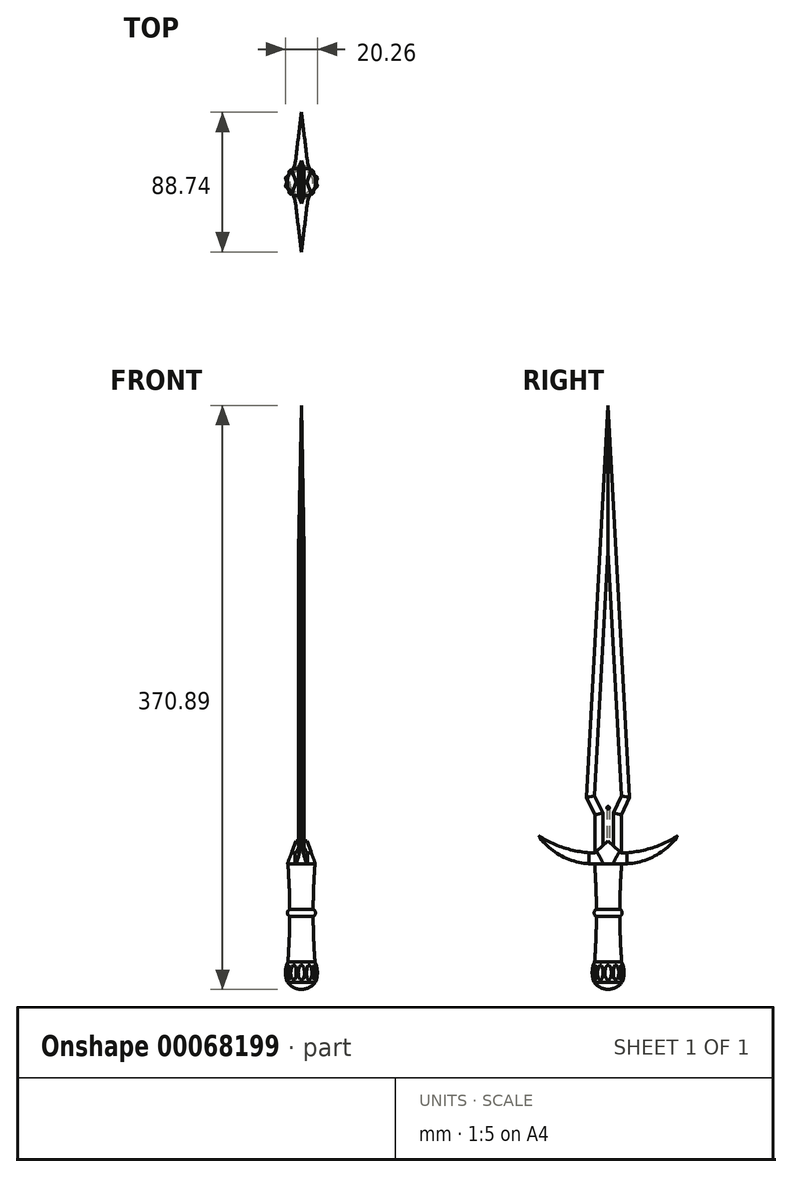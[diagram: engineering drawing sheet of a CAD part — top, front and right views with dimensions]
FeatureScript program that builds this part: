
annotation { "Feature Type Name" : "Feature", "Feature Type Description" : "" }
export const myFeature = defineFeature(function(context is Context, id is Id, definition is map)
    precondition{}
    {
        {
            var Q0;
            Q0=qCreatedBy(makeId("Right.planeOp"),FACE);
            var sketch = newSketch(context, id + "F0", { "sketchPlane" : qUnion([Q0])});
            skLineSegment(sketch, "E0", {"start": v(0, 0) * mm, "end": v(0, -62.4) * mm});
            skLineSegment(sketch, "E1", {"start": v(0, -62.4) * mm, "end": v(-8.58, -62.4) * mm});
            skLineSegment(sketch, "E2", {"start": v(0, 0) * mm, "end": v(-8.58, 0) * mm});
            skLineSegment(sketch, "E3.MirrorCS", {"start": v(0, 0) * mm, "end": v(8.58, 0) * mm});
            skLineSegment(sketch, "E4.MirrorCS", {"start": v(0, -62.4) * mm, "end": v(8.58, -62.4) * mm});
            skPoint(sketch, "E5.MirrorCS.end.orphan", {"position": v(8.58, 0) * mm});
            skPoint(sketch, "E5.MirrorCS.start.orphan", {"position": v(8.58, -62.4) * mm});
            skArc(sketch, "E6", {"start": v(8.58, 0) * mm, "mid": v(7.46, -31.2) * mm, "end": v(8.58, -62.4) * mm});
            skArc(sketch, "E7.MirrorCS", {"start": v(-8.58, 0) * mm, "mid": v(-7.46, -31.2) * mm, "end": v(-8.58, -62.4) * mm});
            skSolve(sketch);
        }
        {
            var Q0;
            Q0=makeQuery(id+"F0.imprint","IMPRINT",FACE,{"disambiguationData":[TD([[makeQuery(id+"F0.imprint","IMPRINT",EDGE,{"derivedFrom":sQuery(id+"F0.wireOp",EDGE,"E0")}),-1.0]])]});
            var Q1;
            Q1=sQuery(id+"F0.wireOp",EDGE,"E0");
            revolve(context, id + "F1", {"entities" : qUnion([Q0]), "axis" : qUnion([Q1]), "revolveType" : RevolveType.FULL});
        }
        {
            var Q0;
            Q0=qCreatedBy(makeId("Front.planeOp"),FACE);
            var sketch = newSketch(context, id + "F2", { "sketchPlane" : qUnion([Q0])});
            skArc(sketch, "E8", {"start": v(-8.58, -62.4) * mm, "mid": v(-6.45, -31.2) * mm, "end": v(-8.58, 0) * mm});
            skCircle(sketch, "E9", {"center": v(-6.45, -31.2) * mm, "radius": 2.43 * mm});
            skLineSegment(sketch, "E10", {"start": v(0, 0) * mm, "end": v(0, -35.93) * mm});
            skSolve(sketch);
        }
        {
            var Q0;
            {var subQ0=sQuery(id+"F2.wireOp",EDGE,"E9");var subQ1=sQuery(id+"F2.wireOp",EDGE,"E8");var subQ2=makeQuery(id+"F2.imprint","INTERSECT",VERTEX,{"disambiguationData":[OD(0.0)],"derivedFrom":[subQ1,subQ0]});Q0=makeQuery(id+"F2.imprint","IMPRINT",FACE,{"disambiguationData":[TD([[makeQuery(id+"F2.imprint","IMPRINT",EDGE,{"disambiguationData":[TD([[subQ2,-1.0]])],"derivedFrom":subQ1}),1.0]])]});}
            var Q1;
            Q1=sQuery(id+"F2.wireOp",EDGE,"E10");
            revolve(context, id + "F3", {"operationType" : NewBodyOperationType.ADD, "entities" : qUnion([Q0]), "axis" : qUnion([Q1]), "revolveType" : RevolveType.FULL});
        }
        {
            var Q0;
            Q0=qCreatedBy(makeId("Front.planeOp"),FACE);
            var sketch = newSketch(context, id + "F4", { "sketchPlane" : qUnion([Q0])});
            skLineSegment(sketch, "E11.0", {"start": v(-8.58, -62.4) * mm, "end": v(8.58, -62.4) * mm});
            skArc(sketch, "E12", {"start": v(-8.58, -62.4) * mm, "mid": v(-10.33, -68.79) * mm, "end": v(-8.87, -75.25) * mm});
            skLineSegment(sketch, "E13", {"start": v(0, -62.4) * mm, "end": v(0, -66.92) * mm});
            skArc(sketch, "E14.MirrorCS", {"start": v(8.58, -62.4) * mm, "mid": v(10.33, -68.79) * mm, "end": v(8.87, -75.25) * mm});
            skArc(sketch, "E15", {"start": v(-8.87, -75.25) * mm, "mid": v(0, -79.74) * mm, "end": v(8.87, -75.25) * mm});
            skLineSegment(sketch, "E16", {"start": v(0, -66.92) * mm, "end": v(0, -79.74) * mm});
            skSolve(sketch);
        }
        {
            var Q0;
            {var subQ1=sQuery(id+"F4.wireOp",EDGE,"E12");Q0=makeQuery(id+"F4.imprint","IMPRINT",FACE,{"disambiguationData":[TD([[makeQuery(id+"F4.imprint","IMPRINT",EDGE,{"derivedFrom":subQ1}),1.0]])]});}
            var Q1;
            Q1=sQuery(id+"F4.wireOp",EDGE,"E16");
            revolve(context, id + "F5", {"entities" : qUnion([Q0]), "axis" : qUnion([Q1]), "revolveType" : RevolveType.FULL});
        }
        {
            var Q0;
            Q0=makeQuery(id+"F5.opRevolve","SWEPT_FACE",FACE,{"disambiguationData":[OSD([sQuery(id+"F4.wireOp",EDGE,"E11.0")])]});
            var sketch = newSketch(context, id + "F6", { "sketchPlane" : qUnion([Q0])});
            skCircle(sketch, "E17.0.0", {"center": v(0, 0) * mm, "radius": 8.58 * mm});
            skCircle(sketch, "E18", {"center": v(0, 0) * mm, "radius": 10.33 * mm});
            skArc(sketch, "E19", {"start": v(-2.02, 10.13) * mm, "mid": v(0, 9.5) * mm, "end": v(2.02, 10.13) * mm});
            skArc(sketch, "E20.1.0", {"start": v(-6.82, 7.77) * mm, "mid": v(-4.75, 8.22) * mm, "end": v(-3.32, 9.79) * mm});
            skArc(sketch, "E20.2.0", {"start": v(-9.79, 3.32) * mm, "mid": v(-8.22, 4.75) * mm, "end": v(-7.77, 6.82) * mm});
            skArc(sketch, "E20.3.0", {"start": v(-10.13, -2.02) * mm, "mid": v(-9.5, 0) * mm, "end": v(-10.13, 2.02) * mm});
            skArc(sketch, "E20.4.0", {"start": v(-7.77, -6.82) * mm, "mid": v(-8.22, -4.75) * mm, "end": v(-9.79, -3.32) * mm});
            skArc(sketch, "E20.5.0", {"start": v(-3.32, -9.79) * mm, "mid": v(-4.75, -8.22) * mm, "end": v(-6.82, -7.77) * mm});
            skArc(sketch, "E20.6.0", {"start": v(2.02, -10.13) * mm, "mid": v(0, -9.5) * mm, "end": v(-2.02, -10.13) * mm});
            skArc(sketch, "E20.7.0", {"start": v(6.82, -7.77) * mm, "mid": v(4.75, -8.22) * mm, "end": v(3.32, -9.79) * mm});
            skArc(sketch, "E20.8.0", {"start": v(9.79, -3.32) * mm, "mid": v(8.22, -4.75) * mm, "end": v(7.77, -6.82) * mm});
            skArc(sketch, "E20.9.0", {"start": v(10.13, 2.02) * mm, "mid": v(9.5, 0) * mm, "end": v(10.13, -2.02) * mm});
            skArc(sketch, "E20.10.0", {"start": v(7.77, 6.82) * mm, "mid": v(8.22, 4.75) * mm, "end": v(9.79, 3.32) * mm});
            skArc(sketch, "E20.11.0", {"start": v(3.32, 9.79) * mm, "mid": v(4.75, 8.22) * mm, "end": v(6.82, 7.77) * mm});
            skSolve(sketch);
        }
        {
            var Q0;
            {var subQ0=sQuery(id+"F6.wireOp",EDGE,"E20.10.0");Q0=makeQuery(id+"F6.imprint","IMPRINT",FACE,{"disambiguationData":[TD([[makeQuery(id+"F6.imprint","IMPRINT",EDGE,{"derivedFrom":subQ0}),1.0]])]});}
            var Q1;
            {var subQ0=sQuery(id+"F6.wireOp",EDGE,"E20.11.0");Q1=makeQuery(id+"F6.imprint","IMPRINT",FACE,{"disambiguationData":[TD([[makeQuery(id+"F6.imprint","IMPRINT",EDGE,{"derivedFrom":subQ0}),1.0]])]});}
            var Q2;
            {var subQ0=sQuery(id+"F6.wireOp",EDGE,"E19");Q2=makeQuery(id+"F6.imprint","IMPRINT",FACE,{"disambiguationData":[TD([[makeQuery(id+"F6.imprint","IMPRINT",EDGE,{"derivedFrom":subQ0}),1.0]])]});}
            var Q3;
            {var subQ0=sQuery(id+"F6.wireOp",EDGE,"E20.1.0");Q3=makeQuery(id+"F6.imprint","IMPRINT",FACE,{"disambiguationData":[TD([[makeQuery(id+"F6.imprint","IMPRINT",EDGE,{"derivedFrom":subQ0}),1.0]])]});}
            var Q4;
            {var subQ0=sQuery(id+"F6.wireOp",EDGE,"E20.2.0");Q4=makeQuery(id+"F6.imprint","IMPRINT",FACE,{"disambiguationData":[TD([[makeQuery(id+"F6.imprint","IMPRINT",EDGE,{"derivedFrom":subQ0}),1.0]])]});}
            var Q5;
            {var subQ0=sQuery(id+"F6.wireOp",EDGE,"E20.3.0");Q5=makeQuery(id+"F6.imprint","IMPRINT",FACE,{"disambiguationData":[TD([[makeQuery(id+"F6.imprint","IMPRINT",EDGE,{"derivedFrom":subQ0}),1.0]])]});}
            var Q6;
            {var subQ0=sQuery(id+"F6.wireOp",EDGE,"E20.4.0");Q6=makeQuery(id+"F6.imprint","IMPRINT",FACE,{"disambiguationData":[TD([[makeQuery(id+"F6.imprint","IMPRINT",EDGE,{"derivedFrom":subQ0}),1.0]])]});}
            var Q7;
            {var subQ0=sQuery(id+"F6.wireOp",EDGE,"E20.5.0");Q7=makeQuery(id+"F6.imprint","IMPRINT",FACE,{"disambiguationData":[TD([[makeQuery(id+"F6.imprint","IMPRINT",EDGE,{"derivedFrom":subQ0}),1.0]])]});}
            var Q8;
            {var subQ0=sQuery(id+"F6.wireOp",EDGE,"E20.6.0");Q8=makeQuery(id+"F6.imprint","IMPRINT",FACE,{"disambiguationData":[TD([[makeQuery(id+"F6.imprint","IMPRINT",EDGE,{"derivedFrom":subQ0}),1.0]])]});}
            var Q9;
            {var subQ0=sQuery(id+"F6.wireOp",EDGE,"E20.7.0");Q9=makeQuery(id+"F6.imprint","IMPRINT",FACE,{"disambiguationData":[TD([[makeQuery(id+"F6.imprint","IMPRINT",EDGE,{"derivedFrom":subQ0}),1.0]])]});}
            var Q10;
            {var subQ0=sQuery(id+"F6.wireOp",EDGE,"E20.8.0");Q10=makeQuery(id+"F6.imprint","IMPRINT",FACE,{"disambiguationData":[TD([[makeQuery(id+"F6.imprint","IMPRINT",EDGE,{"derivedFrom":subQ0}),1.0]])]});}
            var Q11;
            {var subQ0=sQuery(id+"F6.wireOp",EDGE,"E20.9.0");Q11=makeQuery(id+"F6.imprint","IMPRINT",FACE,{"disambiguationData":[TD([[makeQuery(id+"F6.imprint","IMPRINT",EDGE,{"derivedFrom":subQ0}),1.0]])]});}
            extrude(context, id + "F7", {"entities" : qUnion([Q0, Q1, Q2, Q3, Q4, Q5, Q6, Q7, Q8, Q9, Q10, Q11]), "operationType" : NewBodyOperationType.REMOVE, "oppositeDirection" : true, "depth" : 25.4 * mm});
        }
        {
            var Q0;
            Q0=qCreatedBy(makeId("Right.planeOp"),FACE);
            var sketch = newSketch(context, id + "F8", { "sketchPlane" : qUnion([Q0])});
            skLineSegment(sketch, "E21", {"start": v(0, 0) * mm, "end": v(9.73, 0) * mm});
            skLineSegment(sketch, "E22", {"start": v(0, 0) * mm, "end": v(0, 14.65) * mm});
            skLineSegment(sketch, "E23", {"start": v(0, 14.65) * mm, "end": v(8.43, 6.87) * mm});
            skLineSegment(sketch, "E24.MirrorCS", {"start": v(0, 14.65) * mm, "end": v(-8.43, 6.87) * mm});
            skLineSegment(sketch, "E25.MirrorCS", {"start": v(0, 0) * mm, "end": v(-9.73, 0) * mm});
            skArc(sketch, "E26", {"start": v(9.73, 0) * mm, "mid": v(29.23, 4.75) * mm, "end": v(44.37, 17.95) * mm});
            skArc(sketch, "E27", {"start": v(8.43, 6.87) * mm, "mid": v(27.18, 9.87) * mm, "end": v(44.37, 17.95) * mm});
            skArc(sketch, "E28.MirrorCS", {"start": v(-9.73, 0) * mm, "mid": v(-29.23, 4.75) * mm, "end": v(-44.37, 17.95) * mm});
            skArc(sketch, "E29.MirrorCS", {"start": v(-8.43, 6.87) * mm, "mid": v(-27.18, 9.87) * mm, "end": v(-44.37, 17.95) * mm});
            skSolve(sketch);
        }
        {
            var Q0;
            Q0 = qSketchRegion(id + "F8", true);
            extrude(context, id + "F9", {"entities" : qUnion([Q0]), "endBound" : BoundingType.SYMMETRIC, "depth" : 17.78 * mm});
        }
        {
            var Q0;
            Q0=makeQuery(id+"F9.opExtrude","SWEPT_FACE",FACE,{"disambiguationData":[OSD([sQuery(id+"F8.wireOp",EDGE,"E21"),sQuery(id+"F8.wireOp",EDGE,"E25.MirrorCS")])]});
            var sketch = newSketch(context, id + "F10", { "sketchPlane" : qUnion([Q0])});
            skLineSegment(sketch, "E30.0.0", {"start": v(-8.9, 44.37) * mm, "end": v(-8.9, 9.73) * mm});
            skLineSegment(sketch, "E30.0.1", {"start": v(-8.89, 9.73) * mm, "end": v(8.9, 9.73) * mm});
            skLineSegment(sketch, "E30.0.2", {"start": v(8.9, 9.73) * mm, "end": v(8.9, 44.37) * mm});
            skLineSegment(sketch, "E30.0.3", {"start": v(8.9, 44.37) * mm, "end": v(-8.89, 44.37) * mm});
            skLineSegment(sketch, "E31.0.0", {"start": v(-8.9, -9.73) * mm, "end": v(-8.9, -44.37) * mm});
            skLineSegment(sketch, "E31.0.1", {"start": v(-8.89, -44.37) * mm, "end": v(8.9, -44.37) * mm});
            skLineSegment(sketch, "E31.0.2", {"start": v(8.9, -44.37) * mm, "end": v(8.9, -9.73) * mm});
            skLineSegment(sketch, "E31.0.3", {"start": v(8.9, -9.73) * mm, "end": v(-8.89, -9.73) * mm});
            skLineSegment(sketch, "E32", {"start": v(-8.9, 9.73) * mm, "end": v(0, 44.37) * mm});
            skLineSegment(sketch, "E33", {"start": v(0, 44.37) * mm, "end": v(8.89, 9.73) * mm});
            skLineSegment(sketch, "E34", {"start": v(-8.9, -9.73) * mm, "end": v(0, -44.37) * mm});
            skLineSegment(sketch, "E35", {"start": v(0, -44.37) * mm, "end": v(8.89, -9.73) * mm});
            skLineSegment(sketch, "E36", {"start": v(0, 0) * mm, "end": v(0, 6.63) * mm});
            skLineSegment(sketch, "E37", {"start": v(0, 6.63) * mm, "end": v(0, 0) * mm});
            skLineSegment(sketch, "E38", {"start": v(0, 0) * mm, "end": v(-4.77, 0) * mm});
            skPoint(sketch, "E39.MirrorCS.end.orphan", {"position": v(0, 44.37) * mm});
            skPoint(sketch, "E39.MirrorCS.start.orphan", {"position": v(8.89, 9.73) * mm});
            skLineSegment(sketch, "E40", {"start": v(-3.95, 12.01) * mm, "end": v(0, 44.37) * mm});
            skLineSegment(sketch, "E41.MirrorCS", {"start": v(3.95, 12.01) * mm, "end": v(0, 44.37) * mm});
            skLineSegment(sketch, "E42.MirrorCS", {"start": v(-3.95, -12.01) * mm, "end": v(0, -44.37) * mm});
            skLineSegment(sketch, "E43.MirrorCS", {"start": v(3.95, -12.01) * mm, "end": v(0, -44.37) * mm});
            skArc(sketch, "E44", {"start": v(-8.9, 3.2) * mm, "mid": v(-5.94, 7.34) * mm, "end": v(-3.95, 12.01) * mm});
            skLineSegment(sketch, "E45", {"start": v(-8.89, 9.73) * mm, "end": v(-8.89, 3.2) * mm});
            skArc(sketch, "E46.MirrorCS", {"start": v(8.9, 3.2) * mm, "mid": v(5.94, 7.34) * mm, "end": v(3.95, 12.01) * mm});
            skLineSegment(sketch, "E47.MirrorCS", {"start": v(8.89, 9.73) * mm, "end": v(8.89, 3.2) * mm});
            skArc(sketch, "E48.MirrorCS", {"start": v(-8.9, -3.2) * mm, "mid": v(-5.94, -7.34) * mm, "end": v(-3.95, -12.01) * mm});
            skArc(sketch, "E49.MirrorCS", {"start": v(8.9, -3.2) * mm, "mid": v(5.94, -7.34) * mm, "end": v(3.95, -12.01) * mm});
            skLineSegment(sketch, "E50.MirrorCS", {"start": v(8.89, -9.73) * mm, "end": v(8.89, -3.2) * mm});
            skLineSegment(sketch, "E51.MirrorCS", {"start": v(-8.89, -9.73) * mm, "end": v(-8.89, -3.2) * mm});
            skPoint(sketch, "E52.orphan", {"position": v(3.95, -12.01) * mm});
            skPoint(sketch, "E53.MirrorCS.start.orphan", {"position": v(5.5, -9.73) * mm});
            skPoint(sketch, "E54.orphan", {"position": v(-3.95, -12.01) * mm});
            skPoint(sketch, "E55.MirrorCS.start.orphan", {"position": v(-5.5, -9.73) * mm});
            skPoint(sketch, "E56.orphan", {"position": v(-5.5, 9.73) * mm});
            skPoint(sketch, "E57.orphan", {"position": v(5.5, 9.73) * mm});
            skPoint(sketch, "E58.MirrorCS.end.orphan", {"position": v(3.95, 12.01) * mm});
            skSolve(sketch);
        }
        {
            var Q0;
            {var subQ0=sQuery(id+"F10.wireOp",EDGE,"E35");Q0=makeQuery(id+"F10.imprint","IMPRINT",FACE,{"disambiguationData":[TD([[makeQuery(id+"F10.imprint","IMPRINT",EDGE,{"derivedFrom":subQ0}),1.0]])]});}
            var Q1;
            {var subQ0=sQuery(id+"F10.wireOp",EDGE,"E34");Q1=makeQuery(id+"F10.imprint","IMPRINT",FACE,{"disambiguationData":[TD([[makeQuery(id+"F10.imprint","IMPRINT",EDGE,{"derivedFrom":subQ0}),1.0]])]});}
            var Q2;
            {var subQ0=sQuery(id+"F10.wireOp",EDGE,"E31.0.2");Q2=makeQuery(id+"F10.imprint","IMPRINT",FACE,{"disambiguationData":[TD([[makeQuery(id+"F10.imprint","IMPRINT",EDGE,{"derivedFrom":subQ0}),1.0]])]});}
            var Q3;
            {var subQ0=sQuery(id+"F10.wireOp",EDGE,"E31.0.0");Q3=makeQuery(id+"F10.imprint","IMPRINT",FACE,{"disambiguationData":[TD([[makeQuery(id+"F10.imprint","IMPRINT",EDGE,{"derivedFrom":subQ0}),1.0]])]});}
            var Q4;
            {var subQ0=sQuery(id+"F10.wireOp",EDGE,"E32");Q4=makeQuery(id+"F10.imprint","IMPRINT",FACE,{"disambiguationData":[TD([[makeQuery(id+"F10.imprint","IMPRINT",EDGE,{"derivedFrom":subQ0}),-1.0]])]});}
            var Q5;
            {var subQ0=sQuery(id+"F10.wireOp",EDGE,"E33");Q5=makeQuery(id+"F10.imprint","IMPRINT",FACE,{"disambiguationData":[TD([[makeQuery(id+"F10.imprint","IMPRINT",EDGE,{"derivedFrom":subQ0}),-1.0]])]});}
            var Q6;
            {var subQ0=sQuery(id+"F10.wireOp",EDGE,"E30.0.2");Q6=makeQuery(id+"F10.imprint","IMPRINT",FACE,{"disambiguationData":[TD([[makeQuery(id+"F10.imprint","IMPRINT",EDGE,{"derivedFrom":subQ0}),1.0]])]});}
            var Q7;
            {var subQ0=sQuery(id+"F10.wireOp",EDGE,"E30.0.0");Q7=makeQuery(id+"F10.imprint","IMPRINT",FACE,{"disambiguationData":[TD([[makeQuery(id+"F10.imprint","IMPRINT",EDGE,{"derivedFrom":subQ0}),1.0]])]});}
            var Q8;
            {var subQ0=sQuery(id+"F10.wireOp",EDGE,"E47.MirrorCS");Q8=makeQuery(id+"F10.imprint","IMPRINT",FACE,{"disambiguationData":[TD([[makeQuery(id+"F10.imprint","IMPRINT",EDGE,{"derivedFrom":subQ0}),-1.0]])]});}
            var Q9;
            {var subQ0=sQuery(id+"F10.wireOp",EDGE,"E45");Q9=makeQuery(id+"F10.imprint","IMPRINT",FACE,{"disambiguationData":[TD([[makeQuery(id+"F10.imprint","IMPRINT",EDGE,{"derivedFrom":subQ0}),1.0]])]});}
            var Q10;
            {var subQ0=sQuery(id+"F10.wireOp",EDGE,"E51.MirrorCS");Q10=makeQuery(id+"F10.imprint","IMPRINT",FACE,{"disambiguationData":[TD([[makeQuery(id+"F10.imprint","IMPRINT",EDGE,{"derivedFrom":subQ0}),1.0]])]});}
            var Q11;
            {var subQ0=sQuery(id+"F10.wireOp",EDGE,"E50.MirrorCS");Q11=makeQuery(id+"F10.imprint","IMPRINT",FACE,{"disambiguationData":[TD([[makeQuery(id+"F10.imprint","IMPRINT",EDGE,{"derivedFrom":subQ0}),-1.0]])]});}
            extrude(context, id + "F11", {"entities" : qUnion([Q0, Q1, Q2, Q3, Q4, Q5, Q6, Q7, Q8, Q9, Q10, Q11]), "operationType" : NewBodyOperationType.REMOVE, "oppositeDirection" : true, "depth" : 25.4 * mm});
        }
        {
            var Q0;
            Q0=qCreatedBy(makeId("Front.planeOp"),FACE);
            cPlane(context, id + "F12", {"entities" : qUnion([Q0]), "cplaneType" : CPlaneType.OFFSET, "offset" : 152.4 * mm, "width" : 152.4 * mm, "height" : 152.4 * mm});
        }
        {
            var Q0;
            Q0=qCreatedBy(id+"F12.planeOp",FACE);
            var sketch = newSketch(context, id + "F13", { "sketchPlane" : qUnion([Q0])});
            skPoint(sketch, "E59.0", {"position": v(-8.9, 0) * mm});
            skLineSegment(sketch, "E60.0", {"start": v(8.9, 14.65) * mm, "end": v(-8.89, 14.65) * mm});
            skPoint(sketch, "E61.0", {"position": v(8.9, 0) * mm});
            skLineSegment(sketch, "E62", {"start": v(-8.9, 0) * mm, "end": v(-3.42, 14.65) * mm});
            skLineSegment(sketch, "E63", {"start": v(0, 0) * mm, "end": v(0, -10.04) * mm});
            skLineSegment(sketch, "E64", {"start": v(-8.9, 0) * mm, "end": v(-8.89, 14.65) * mm});
            skLineSegment(sketch, "E65.MirrorCS", {"start": v(8.9, 0) * mm, "end": v(3.42, 14.65) * mm});
            skLineSegment(sketch, "E66.MirrorCS", {"start": v(8.9, 0) * mm, "end": v(8.89, 14.65) * mm});
            skSolve(sketch);
        }
        {
            var Q0;
            Q0 = qSketchRegion(id + "F13", true);
            extrude(context, id + "F14", {"entities" : qUnion([Q0]), "operationType" : NewBodyOperationType.REMOVE, "endBound" : BoundingType.THROUGH_ALL, "oppositeDirection" : true, "depth" : 25.4 * mm});
        }
        {
            var Q0;
            Q0=qCreatedBy(makeId("Right.planeOp"),FACE);
            var sketch = newSketch(context, id + "F15", { "sketchPlane" : qUnion([Q0])});
            skLineSegment(sketch, "E67.0", {"start": v(0, 14.65) * mm, "end": v(7.33, 7.88) * mm});
            skLineSegment(sketch, "E68.0", {"start": v(8.43, 6.87) * mm, "end": v(7.33, 7.88) * mm});
            skLineSegment(sketch, "E69.0", {"start": v(0, 14.65) * mm, "end": v(-7.33, 7.88) * mm});
            skLineSegment(sketch, "E70.0", {"start": v(-7.33, 7.88) * mm, "end": v(-8.43, 6.87) * mm});
            skLineSegment(sketch, "E71", {"start": v(8.43, 6.87) * mm, "end": v(8.43, 31.1) * mm});
            skLineSegment(sketch, "E72", {"start": v(-8.43, 6.87) * mm, "end": v(-8.43, 31.1) * mm});
            skLineSegment(sketch, "E73", {"start": v(0, 14.65) * mm, "end": v(0, 291.15) * mm});
            skLineSegment(sketch, "E74", {"start": v(8.43, 31.1) * mm, "end": v(13.7, 42.02) * mm});
            skLineSegment(sketch, "E75", {"start": v(13.7, 42.02) * mm, "end": v(0, 291.15) * mm});
            skLineSegment(sketch, "E76.MirrorCS", {"start": v(-13.7, 42.02) * mm, "end": v(0, 291.15) * mm});
            skLineSegment(sketch, "E77.MirrorCS", {"start": v(-8.43, 31.1) * mm, "end": v(-13.7, 42.02) * mm});
            skSolve(sketch);
        }
        {
            var Q0;
            Q0 = qSketchRegion(id + "F15", true);
            extrude(context, id + "F16", {"entities" : qUnion([Q0]), "endBound" : BoundingType.SYMMETRIC, "depth" : 3.56 * mm});
        }
        {
            var Q0;
            Q0=makeQuery(id+"F16.opExtrude","CAP_EDGE",EDGE,{"disambiguationData":[OSD([sQuery(id+"F15.wireOp",EDGE,"E75")])],"isStart":true});
            var Q1;
            Q1=makeQuery(id+"F16.opExtrude","CAP_EDGE",EDGE,{"disambiguationData":[OSD([sQuery(id+"F15.wireOp",EDGE,"E76.MirrorCS")])],"isStart":true});
            var Q2;
            Q2=makeQuery(id+"F16.opExtrude","CAP_EDGE",EDGE,{"disambiguationData":[OSD([sQuery(id+"F15.wireOp",EDGE,"E74")])],"isStart":true});
            var Q3;
            Q3=makeQuery(id+"F16.opExtrude","CAP_EDGE",EDGE,{"disambiguationData":[OSD([sQuery(id+"F15.wireOp",EDGE,"E77.MirrorCS")])],"isStart":true});
            var Q4;
            Q4=makeQuery(id+"F16.opExtrude","CAP_EDGE",EDGE,{"disambiguationData":[OSD([sQuery(id+"F15.wireOp",EDGE,"E72")])],"isStart":true});
            var Q5;
            Q5=makeQuery(id+"F16.opExtrude","CAP_EDGE",EDGE,{"disambiguationData":[OSD([sQuery(id+"F15.wireOp",EDGE,"E71")])],"isStart":true});
            chamfer(context, id + "F17", {"entities" : qUnion([Q0, Q1, Q2, Q3, Q4, Q5]), "chamferType" : ChamferType.TWO_OFFSETS, "width1" : 1.78 * mm, "oppositeDirection" : false, "width2" : 5.08 * mm, "tangentPropagation" : true});
        }
        {
            var Q0;
            Q0=makeQuery(id+"F16.opExtrude","CAP_EDGE",EDGE,{"disambiguationData":[OSD([sQuery(id+"F15.wireOp",EDGE,"E75")])],"isStart":false});
            var Q1;
            Q1=makeQuery(id+"F16.opExtrude","CAP_EDGE",EDGE,{"disambiguationData":[OSD([sQuery(id+"F15.wireOp",EDGE,"E76.MirrorCS")])],"isStart":false});
            var Q2;
            Q2=makeQuery(id+"F16.opExtrude","CAP_EDGE",EDGE,{"disambiguationData":[OSD([sQuery(id+"F15.wireOp",EDGE,"E74")])],"isStart":false});
            var Q3;
            Q3=makeQuery(id+"F16.opExtrude","CAP_EDGE",EDGE,{"disambiguationData":[OSD([sQuery(id+"F15.wireOp",EDGE,"E77.MirrorCS")])],"isStart":false});
            var Q4;
            Q4=makeQuery(id+"F16.opExtrude","CAP_EDGE",EDGE,{"disambiguationData":[OSD([sQuery(id+"F15.wireOp",EDGE,"E72")])],"isStart":false});
            var Q5;
            Q5=makeQuery(id+"F16.opExtrude","CAP_EDGE",EDGE,{"disambiguationData":[OSD([sQuery(id+"F15.wireOp",EDGE,"E71")])],"isStart":false});
            chamfer(context, id + "F18", {"entities" : qUnion([Q0, Q1, Q2, Q3, Q4, Q5]), "chamferType" : ChamferType.TWO_OFFSETS, "width1" : 5.08 * mm, "oppositeDirection" : false, "width2" : 1.78 * mm, "tangentPropagation" : true});
        }
        {
            var Q0;
            Q0=makeQuery(id+"F1.opRevolve","SWEPT_FACE",FACE,{"disambiguationData":[OSD([sQuery(id+"F0.wireOp",EDGE,"E2")])]});
            var sketch = newSketch(context, id + "F19", { "sketchPlane" : qUnion([Q0])});
            skLineSegment(sketch, "E78.0", {"start": v(-1.78, 0) * mm, "end": v(-1.78, -3.35) * mm});
            skLineSegment(sketch, "E79.0.0", {"start": v(-1.78, 3.35) * mm, "end": v(0, 8.43) * mm});
            skLineSegment(sketch, "E79.0.1", {"start": v(0, 8.43) * mm, "end": v(1.78, 3.35) * mm});
            skLineSegment(sketch, "E79.0.2", {"start": v(1.78, 3.35) * mm, "end": v(1.78, 0) * mm});
            skLineSegment(sketch, "E79.0.3", {"start": v(1.78, 0) * mm, "end": v(-1.78, 0) * mm});
            skLineSegment(sketch, "E79.0.4", {"start": v(-1.78, 0) * mm, "end": v(-1.78, 3.35) * mm});
            skLineSegment(sketch, "E80.0", {"start": v(1.78, 0) * mm, "end": v(1.78, -3.35) * mm});
            skPoint(sketch, "E81.orphan", {"position": v(-1.78, -1.67) * mm});
            skPoint(sketch, "E82.end.orphan", {"position": v(-1.78, 1.67) * mm});
            skLineSegment(sketch, "E83", {"start": v(-1.78, -1.67) * mm, "end": v(-1.78, 0) * mm});
            skLineSegment(sketch, "E84", {"start": v(-1.78, 1.67) * mm, "end": v(-1.78, 0) * mm});
            skArc(sketch, "E85", {"start": v(-1.78, -0.84) * mm, "mid": v(-1.41, 0) * mm, "end": v(-1.78, 0.84) * mm});
            skLineSegment(sketch, "E86", {"start": v(0, 0) * mm, "end": v(0, -1.52) * mm});
            skArc(sketch, "E87.MirrorCS", {"start": v(1.78, -0.84) * mm, "mid": v(1.41, 0) * mm, "end": v(1.78, 0.84) * mm});
            skSolve(sketch);
        }
        {
            var Q0;
            {var subQ0=sQuery(id+"F19.wireOp",EDGE,"E80.0");var subQ3=sQuery(id+"F19.wireOp",EDGE,"E87.MirrorCS");var subQ5=makeQuery(id+"F19.imprint","INTERSECT",VERTEX,{"derivedFrom":[subQ0,subQ3]});Q0=makeQuery(id+"F19.imprint","IMPRINT",FACE,{"disambiguationData":[TD([[makeQuery(id+"F19.imprint","IMPRINT",EDGE,{"disambiguationData":[TD([[subQ5,-1.0]])],"derivedFrom":subQ3}),-1.0]])]});}
            var Q1;
            {var subQ0=sQuery(id+"F19.wireOp",EDGE,"E83");var subQ3=sQuery(id+"F19.wireOp",EDGE,"E85");var subQ5=makeQuery(id+"F19.imprint","INTERSECT",VERTEX,{"derivedFrom":[subQ0,subQ3]});Q1=makeQuery(id+"F19.imprint","IMPRINT",FACE,{"disambiguationData":[TD([[makeQuery(id+"F19.imprint","IMPRINT",EDGE,{"disambiguationData":[TD([[subQ5,-1.0]])],"derivedFrom":subQ3}),1.0]])]});}
            var Q2;
            {var subQ1=sQuery(id+"F19.wireOp",EDGE,"E79.0.2");var subQ3=sQuery(id+"F19.wireOp",EDGE,"E87.MirrorCS");var subQ4=makeQuery(id+"F19.imprint","INTERSECT",VERTEX,{"derivedFrom":[subQ1,subQ3]});Q2=makeQuery(id+"F19.imprint","IMPRINT",FACE,{"disambiguationData":[TD([[makeQuery(id+"F19.imprint","IMPRINT",EDGE,{"disambiguationData":[TD([[subQ4,1.0]])],"derivedFrom":subQ3}),-1.0]])]});}
            var Q3;
            {var subQ0=sQuery(id+"F19.wireOp",EDGE,"E84");var subQ3=sQuery(id+"F19.wireOp",EDGE,"E85");var subQ5=makeQuery(id+"F19.imprint","INTERSECT",VERTEX,{"derivedFrom":[subQ0,subQ3]});Q3=makeQuery(id+"F19.imprint","IMPRINT",FACE,{"disambiguationData":[TD([[makeQuery(id+"F19.imprint","IMPRINT",EDGE,{"disambiguationData":[TD([[subQ5,1.0]])],"derivedFrom":subQ3}),1.0]])]});}
            extrude(context, id + "F20", {"entities" : qUnion([Q0, Q1, Q2, Q3]), "operationType" : NewBodyOperationType.REMOVE, "depth" : 35.56 * mm});
        }
        {
            var Q0;
            Q0=makeQuery(id+"F20.boolean.opBoolean","COPY",FACE,{"derivedFrom":makeQuery(id+"F20.opExtrude","CAP_FACE",FACE,{"disambiguationData":[OSD([sQuery(id+"F19.wireOp",EDGE,"E83"),sQuery(id+"F19.wireOp",EDGE,"E84"),sQuery(id+"F19.wireOp",EDGE,"E85")])],"isStart":false})});
            var sketch = newSketch(context, id + "F21", { "sketchPlane" : qUnion([Q0])});
            skArc(sketch, "E88.0.0", {"start": v(-1.78, -0.84) * mm, "mid": v(-1.41, 0) * mm, "end": v(-1.78, 0.84) * mm});
            skLineSegment(sketch, "E88.0.1", {"start": v(-1.78, 0.84) * mm, "end": v(-1.78, -0.84) * mm});
            skLineSegment(sketch, "E89.0.0", {"start": v(1.78, -0.84) * mm, "end": v(1.78, 0.84) * mm});
            skArc(sketch, "E89.0.1", {"start": v(1.78, 0.84) * mm, "mid": v(1.41, 0) * mm, "end": v(1.78, -0.84) * mm});
            skLineSegment(sketch, "E90", {"start": v(-1.78, 0) * mm, "end": v(1.78, 0) * mm});
            skSolve(sketch);
        }
        {
            var Q0;
            {var subQ0=sQuery(id+"F21.wireOp",EDGE,"E88.0.1");var subQ1=sQuery(id+"F21.wireOp",EDGE,"E88.0.0");var subQ2=makeQuery(id+"F21.imprint","INTERSECT",VERTEX,{"disambiguationData":[OD(0.0)],"derivedFrom":[subQ1,subQ0]});Q0=makeQuery(id+"F21.imprint","IMPRINT",FACE,{"disambiguationData":[TD([[makeQuery(id+"F21.imprint","IMPRINT",EDGE,{"disambiguationData":[TD([[subQ2,-1.0]])],"derivedFrom":subQ1}),-1.0]])]});}
            var Q1;
            {var subQ0=sQuery(id+"F21.wireOp",EDGE,"E89.0.1");var subQ1=sQuery(id+"F21.wireOp",EDGE,"E89.0.0");var subQ2=makeQuery(id+"F21.imprint","INTERSECT",VERTEX,{"disambiguationData":[OD(1.0)],"derivedFrom":[subQ1,subQ0]});Q1=makeQuery(id+"F21.imprint","IMPRINT",FACE,{"disambiguationData":[TD([[makeQuery(id+"F21.imprint","IMPRINT",EDGE,{"disambiguationData":[TD([[subQ2,1.0]])],"derivedFrom":subQ1}),1.0]])]});}
            var Q2;
            Q2=sQuery(id+"F21.wireOp",EDGE,"E90");
            revolve(context, id + "F22", {"operationType" : NewBodyOperationType.REMOVE, "entities" : qUnion([Q0, Q1]), "axis" : qUnion([Q2]), "revolveType" : RevolveType.FULL, "oppositeDirection" : true});
        }
        {
            var Q0;
            Q0=makeQuery(id+"F16.opExtrude","CAP_FACE",FACE,{"disambiguationData":[OSD([sQuery(id+"F15.wireOp",EDGE,"E67.0"),sQuery(id+"F15.wireOp",EDGE,"E68.0"),sQuery(id+"F15.wireOp",EDGE,"E69.0"),sQuery(id+"F15.wireOp",EDGE,"E70.0"),sQuery(id+"F15.wireOp",EDGE,"E71"),sQuery(id+"F15.wireOp",EDGE,"E72"),sQuery(id+"F15.wireOp",EDGE,"E74"),sQuery(id+"F15.wireOp",EDGE,"E75"),sQuery(id+"F15.wireOp",EDGE,"E76.MirrorCS"),sQuery(id+"F15.wireOp",EDGE,"E77.MirrorCS")])],"isStart":true});
            var sketch = newSketch(context, id + "F23", { "sketchPlane" : qUnion([Q0])});
            skLineSegment(sketch, "E91.0", {"start": v(-3.35, 11.56) * mm, "end": v(-8.43, 6.87) * mm});
            skLineSegment(sketch, "E92.0", {"start": v(8.43, 6.87) * mm, "end": v(3.35, 11.56) * mm});
            skLineSegment(sketch, "E93", {"start": v(-5.89, 9.21) * mm, "end": v(-3.35, -67.3) * mm});
            skLineSegment(sketch, "E94", {"start": v(3.35, -67.3) * mm, "end": v(3.35, -69.26) * mm});
            skLineSegment(sketch, "E95", {"start": v(-3.35, -67.3) * mm, "end": v(6.35, -67.3) * mm});
            skLineSegment(sketch, "E96.0", {"start": v(-8.58, -62.4) * mm, "end": v(8.58, -62.4) * mm});
            skLineSegment(sketch, "E97", {"start": v(0, -62.4) * mm, "end": v(0, -67.3) * mm});
            skLineSegment(sketch, "E98", {"start": v(5.89, 9.21) * mm, "end": v(3.35, -67.3) * mm});
            skLineSegment(sketch, "E99", {"start": v(-3.35, 11.56) * mm, "end": v(0, 14.65) * mm});
            skLineSegment(sketch, "E100", {"start": v(0, 14.65) * mm, "end": v(3.35, 11.56) * mm});
            skSolve(sketch);
        }
        {
            var Q0;
            Q0 = qSketchRegion(id + "F23", true);
            extrude(context, id + "F24", {"entities" : qUnion([Q0]), "operationType" : NewBodyOperationType.REMOVE, "oppositeDirection" : true, "depth" : 3.56 * mm});
        }
        {
            var Q0;
            {var subQ2=sQuery(id+"F23.wireOp",EDGE,"E93");var subQ4=sQuery(id+"F23.wireOp",EDGE,"E91.0");var subQ5=makeQuery(id+"F23.imprint","INTERSECT",VERTEX,{"derivedFrom":[subQ4,subQ2]});Q0=makeQuery(id+"F23.imprint","IMPRINT",FACE,{"disambiguationData":[TD([[makeQuery(id+"F23.imprint","IMPRINT",EDGE,{"disambiguationData":[TD([[subQ5,-1.0]])],"derivedFrom":subQ2}),1.0]])]});}
            var Q1;
            {var subQ5=sQuery(id+"F23.wireOp",EDGE,"E97");Q1=makeQuery(id+"F23.imprint","IMPRINT",FACE,{"disambiguationData":[TD([[makeQuery(id+"F23.imprint","IMPRINT",EDGE,{"derivedFrom":subQ5}),-1.0]])]});}
            var Q2;
            {var subQ3=sQuery(id+"F23.wireOp",EDGE,"E97");Q2=makeQuery(id+"F23.imprint","IMPRINT",FACE,{"disambiguationData":[TD([[makeQuery(id+"F23.imprint","IMPRINT",EDGE,{"derivedFrom":subQ3}),1.0]])]});}
            extrude(context, id + "F25", {"entities" : qUnion([Q0, Q1, Q2]), "operationType" : NewBodyOperationType.ADD, "oppositeDirection" : true, "depth" : 3.56 * mm});
        }
    });
